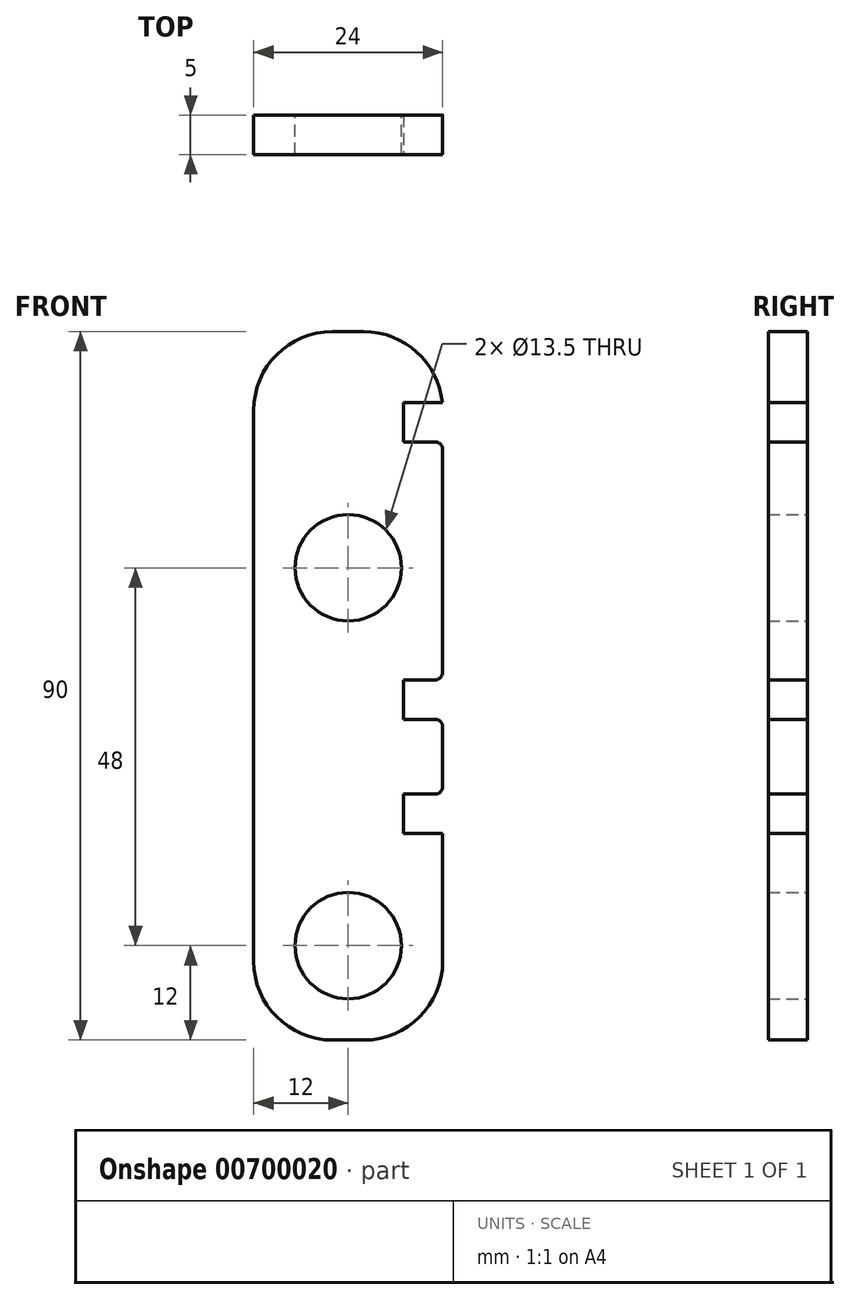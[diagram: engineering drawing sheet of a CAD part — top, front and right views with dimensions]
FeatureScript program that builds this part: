
annotation { "Feature Type Name" : "Feature", "Feature Type Description" : "" }
export const myFeature = defineFeature(function(context is Context, id is Id, definition is map)
    precondition{}
    {
        {
            assignVariable(context, id + "F0", {"name" : "bar_fillet", "anyValue" : 10 * mm});
        }
        {
            assignVariable(context, id + "F1", {"name" : "th", "anyValue" : 5 * mm});
        }
        {
            var Q0;
            Q0=qCreatedBy(makeId("Front.planeOp"),FACE);
            var sketch = newSketch(context, id + "F2", { "sketchPlane" : qUnion([Q0])});
            skLineSegment(sketch, "E0.bottom", {"start": v(0, 0) * mm, "end": v(24, 0) * mm});
            skLineSegment(sketch, "E0.top", {"start": v(0, 90) * mm, "end": v(24, 90) * mm});
            skLineSegment(sketch, "E0.left", {"start": v(0, 0) * mm, "end": v(0, 90) * mm});
            skLineSegment(sketch, "E0.right", {"start": v(24, 0) * mm, "end": v(24, 90) * mm});
            skLineSegment(sketch, "E1", {"start": v(12, 90) * mm, "end": v(12, 0) * mm, "construction": true});
            skCircle(sketch, "E2", {"center": v(12, 60) * mm, "radius": 6.75 * mm});
            skCircle(sketch, "E3", {"center": v(12, 12) * mm, "radius": 6.75 * mm});
            skSolve(sketch);
        }
        {
            var Q0;
            Q0=makeQuery(id+"F2.imprint","IMPRINT",FACE,{"disambiguationData":[TD([[makeQuery(id+"F2.imprint","IMPRINT",EDGE,{"derivedFrom":sQuery(id+"F2.wireOp",EDGE,"E0.bottom")}),1.0]])]});
            extrude(context, id + "F3", {"entities" : qUnion([Q0]), "depth" : getVariable(context, 'th'), "offsetDistance" : 25 * mm});
        }
        {
            var Q0;
            Q0=makeQuery(id+"F3.opExtrude","SWEPT_EDGE",EDGE,{"disambiguationData":[OSD([sQuery(id+"F2.wireOp",EDGE,"E0.top"),sQuery(id+"F2.wireOp",EDGE,"E0.left")])]});
            var Q1;
            Q1=makeQuery(id+"F3.opExtrude","SWEPT_EDGE",EDGE,{"disambiguationData":[OSD([sQuery(id+"F2.wireOp",EDGE,"E0.bottom"),sQuery(id+"F2.wireOp",EDGE,"E0.left")])]});
            var Q2;
            Q2=makeQuery(id+"F3.opExtrude","SWEPT_EDGE",EDGE,{"disambiguationData":[OSD([sQuery(id+"F2.wireOp",EDGE,"E0.top"),sQuery(id+"F2.wireOp",EDGE,"E0.right")])]});
            var Q3;
            Q3=makeQuery(id+"F3.opExtrude","SWEPT_EDGE",EDGE,{"disambiguationData":[OSD([sQuery(id+"F2.wireOp",EDGE,"E0.bottom"),sQuery(id+"F2.wireOp",EDGE,"E0.right")])]});
            fillet(context, id + "F4", {"entities" : qUnion([Q0, Q1, Q2, Q3]), "radius" : getVariable(context, 'bar_fillet'), "tangentPropagation" : true, "allowEdgeOverflow" : false});
        }
        {
            var Q0;
            Q0=makeQuery(id+"F3.opExtrude","CAP_FACE",FACE,{"disambiguationData":[OSD([sQuery(id+"F2.wireOp",EDGE,"E0.bottom"),sQuery(id+"F2.wireOp",EDGE,"E0.top"),sQuery(id+"F2.wireOp",EDGE,"E0.left"),sQuery(id+"F2.wireOp",EDGE,"E0.right"),sQuery(id+"F2.wireOp",EDGE,"E2"),sQuery(id+"F2.wireOp",EDGE,"E3")])],"isStart":false});
            var sketch = newSketch(context, id + "F5", { "sketchPlane" : qUnion([Q0])});
            skLineSegment(sketch, "E4", {"start": v(12, 60) * mm, "end": v(12, 90) * mm, "construction": true});
            skLineSegment(sketch, "E5", {"start": v(12, 78.5) * mm, "end": v(42.8, 78.5) * mm, "construction": true});
            skLineSegment(sketch, "E6.bottom", {"start": v(19, 76) * mm, "end": v(29, 76) * mm});
            skLineSegment(sketch, "E6.top", {"start": v(19, 81) * mm, "end": v(29, 81) * mm});
            skLineSegment(sketch, "E6.left", {"start": v(19, 76) * mm, "end": v(19, 81) * mm});
            skLineSegment(sketch, "E6.right", {"start": v(29, 76) * mm, "end": v(29, 81) * mm});
            skPoint(sketch, "E6.middle", {"position": v(24, 78.5) * mm});
            skLineSegment(sketch, "E7", {"start": v(12, 12) * mm, "end": v(12, 60) * mm, "construction": true});
            skLineSegment(sketch, "E8", {"start": v(12, 43.25) * mm, "end": v(24, 43.25) * mm, "construction": true});
            skPoint(sketch, "E9", {"position": v(12, 53.25) * mm});
            skLineSegment(sketch, "E10.bottom", {"start": v(29, 40.75) * mm, "end": v(19, 40.75) * mm});
            skLineSegment(sketch, "E10.top", {"start": v(29, 45.75) * mm, "end": v(19, 45.75) * mm});
            skLineSegment(sketch, "E10.left", {"start": v(29, 40.75) * mm, "end": v(29, 45.75) * mm});
            skLineSegment(sketch, "E10.right", {"start": v(19, 40.75) * mm, "end": v(19, 45.75) * mm});
            skPoint(sketch, "E10.middle", {"position": v(24, 43.25) * mm});
            skLineSegment(sketch, "E11.bottom", {"start": v(29, 26.25) * mm, "end": v(19, 26.25) * mm});
            skLineSegment(sketch, "E11.top", {"start": v(29, 31.25) * mm, "end": v(19, 31.25) * mm});
            skLineSegment(sketch, "E11.left", {"start": v(29, 26.25) * mm, "end": v(29, 31.25) * mm});
            skLineSegment(sketch, "E11.right", {"start": v(19, 26.25) * mm, "end": v(19, 31.25) * mm});
            skPoint(sketch, "E11.middle", {"position": v(24, 28.75) * mm});
            skLineSegment(sketch, "E12", {"start": v(24, 28.75) * mm, "end": v(12, 28.75) * mm, "construction": true});
            skPoint(sketch, "E13", {"position": v(12, 18.75) * mm});
            skSolve(sketch);
        }
        {
            var Q0;
            {var subQ0=sQuery(id+"F5.wireOp",EDGE,"E6.left");Q0=makeQuery(id+"F5.imprint","IMPRINT",FACE,{"disambiguationData":[TD([[makeQuery(id+"F5.imprint","IMPRINT",EDGE,{"derivedFrom":subQ0}),-1.0]])]});}
            var Q1;
            {var subQ0=sQuery(id+"F5.wireOp",EDGE,"E10.right");Q1=makeQuery(id+"F5.imprint","IMPRINT",FACE,{"disambiguationData":[TD([[makeQuery(id+"F5.imprint","IMPRINT",EDGE,{"derivedFrom":subQ0}),-1.0]])]});}
            var Q2;
            {var subQ0=sQuery(id+"F5.wireOp",EDGE,"E11.right");Q2=makeQuery(id+"F5.imprint","IMPRINT",FACE,{"disambiguationData":[TD([[makeQuery(id+"F5.imprint","IMPRINT",EDGE,{"derivedFrom":subQ0}),-1.0]])]});}
            extrude(context, id + "F6", {"entities" : qUnion([Q0, Q1, Q2]), "operationType" : NewBodyOperationType.REMOVE, "oppositeDirection" : true, "depth" : 25 * mm, "offsetDistance" : 25 * mm});
        }
        {
            var Q0;
            Q0=makeQuery(id+"F6.boolean.opBoolean","COPY",EDGE,{"derivedFrom":makeQuery(id+"F6.opExtrude","SWEPT_EDGE",EDGE,{"disambiguationData":[OSD([sQuery(id+"F2.wireOp",EDGE,"E0.right"),sQuery(id+"F5.wireOp",EDGE,"E11.bottom")])]})});
            var Q1;
            Q1=makeQuery(id+"F6.boolean.opBoolean","COPY",EDGE,{"derivedFrom":makeQuery(id+"F6.opExtrude","SWEPT_EDGE",EDGE,{"disambiguationData":[OSD([sQuery(id+"F2.wireOp",EDGE,"E0.right"),sQuery(id+"F5.wireOp",EDGE,"E11.top")])]})});
            var Q2;
            Q2=makeQuery(id+"F6.boolean.opBoolean","COPY",EDGE,{"derivedFrom":makeQuery(id+"F6.opExtrude","SWEPT_EDGE",EDGE,{"disambiguationData":[OSD([sQuery(id+"F2.wireOp",EDGE,"E0.right"),sQuery(id+"F5.wireOp",EDGE,"E10.bottom")])]})});
            var Q3;
            Q3=makeQuery(id+"F6.boolean.opBoolean","COPY",EDGE,{"derivedFrom":makeQuery(id+"F6.opExtrude","SWEPT_EDGE",EDGE,{"disambiguationData":[OSD([sQuery(id+"F2.wireOp",EDGE,"E0.right"),sQuery(id+"F5.wireOp",EDGE,"E10.top")])]})});
            var Q4;
            Q4=makeQuery(id+"F6.boolean.opBoolean","COPY",EDGE,{"derivedFrom":makeQuery(id+"F6.opExtrude","SWEPT_EDGE",EDGE,{"disambiguationData":[OSD([sQuery(id+"F2.wireOp",EDGE,"E0.right"),sQuery(id+"F5.wireOp",EDGE,"E6.bottom")])]})});
            var Q5;
            Q5=makeQuery(id+"F6.boolean.opBoolean","COPY",EDGE,{"derivedFrom":makeQuery(id+"F6.opExtrude","SWEPT_EDGE",EDGE,{"disambiguationData":[OSD([sQuery(id+"F2.wireOp",EDGE,"E0.bottom"),sQuery(id+"F2.wireOp",EDGE,"E0.top"),sQuery(id+"F2.wireOp",EDGE,"E0.left"),sQuery(id+"F2.wireOp",EDGE,"E0.right"),sQuery(id+"F2.wireOp",EDGE,"E2"),sQuery(id+"F2.wireOp",EDGE,"E3"),sQuery(id+"F5.wireOp",EDGE,"E6.top")])]})});
            fillet(context, id + "F7", {"entities" : qUnion([Q0, Q1, Q2, Q3, Q4, Q5]), "radius" : 1 * mm, "tangentPropagation" : true, "allowEdgeOverflow" : false});
        }
    });
